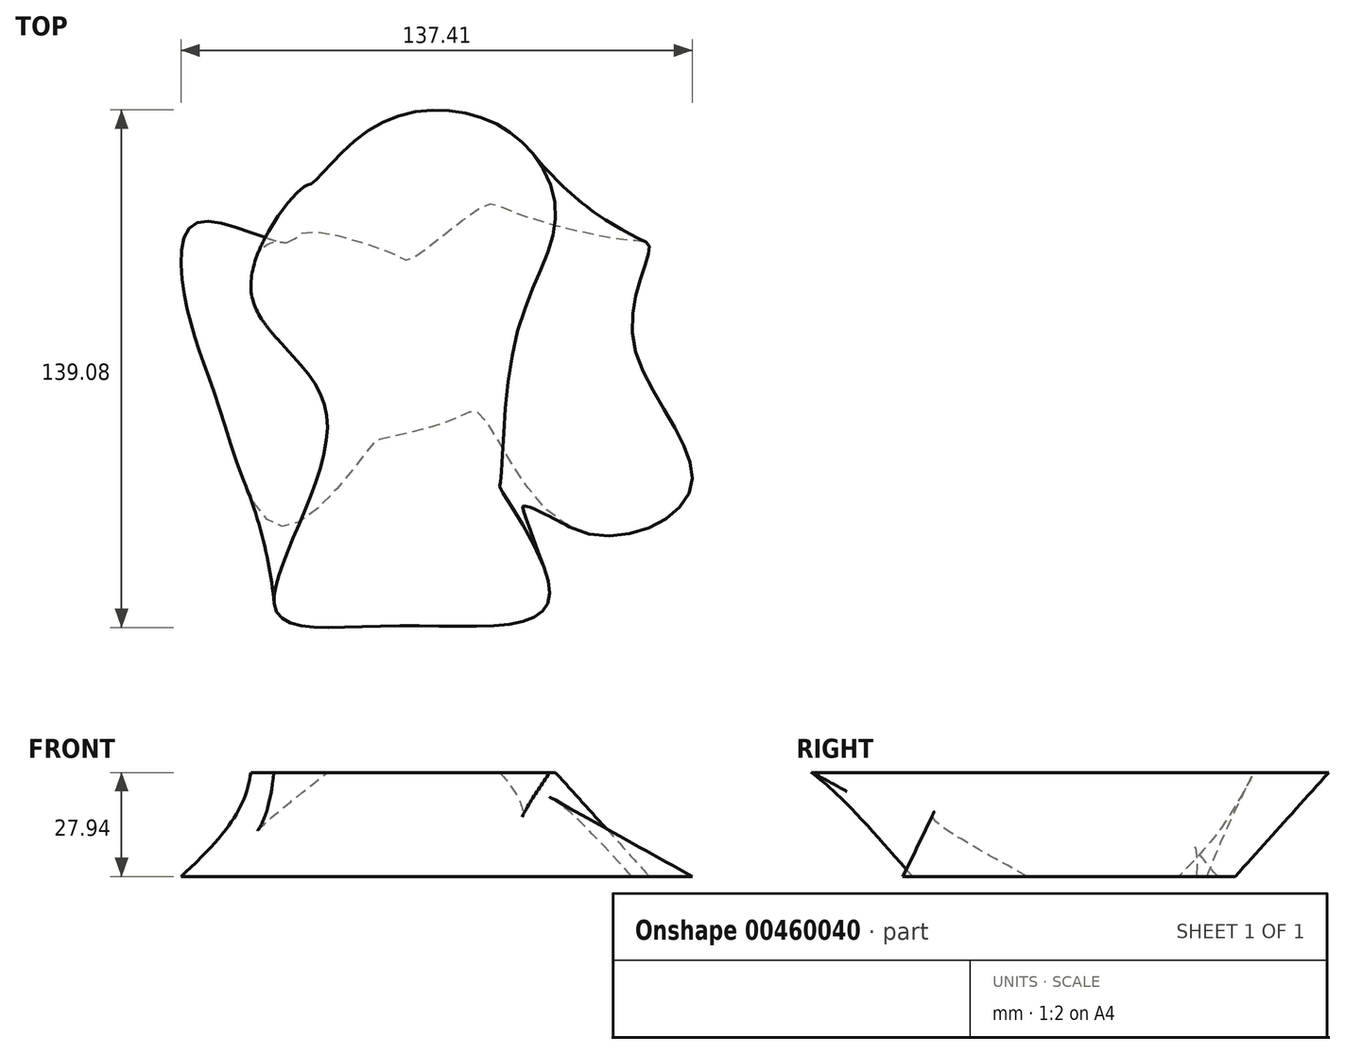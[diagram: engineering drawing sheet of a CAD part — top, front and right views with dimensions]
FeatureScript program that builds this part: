
annotation { "Feature Type Name" : "Feature", "Feature Type Description" : "" }
export const myFeature = defineFeature(function(context is Context, id is Id, definition is map)
    precondition{}
    {
        {
            var Q0;
            Q0=qCreatedBy(makeId("Top.planeOp"),FACE);
            var sketch = newSketch(context, id + "F0", { "sketchPlane" : qUnion([Q0])});
            skFitSpline(sketch, "E0", {"points": [v(-33.51, 29.77) * mm, v(-28.86, 32.46) * mm, v(-3.32, 25.96) * mm, v(0, 25.4) * mm, v(19.83, 39.8) * mm, v(25.33, 38.8) * mm, v(56.94, 30.62) * mm, v(63.85, 28.79) * mm, v(59.48, 3.67) * mm, v(75.14, -35.84) * mm, v(43.4, -47.13) * mm, v(18.13, -16.23) * mm, v(11.64, -17.64) * mm, v(-7.83, -23) * mm, v(-11.22, -25.26) * mm, v(-34.22, -46.57) * mm, v(-51.15, -16.37) * mm, v(-60.75, 13.97) * mm, v(-57.5, 35.14) * mm, v(-33.51, 29.77) * mm]});
            skSolve(sketch);
        }
        {
            var Q0;
            Q0=qCreatedBy(makeId("Top.planeOp"),FACE);
            cPlane(context, id + "F1", {"entities" : qUnion([Q0]), "cplaneType" : CPlaneType.OFFSET, "offset" : 27.94 * mm, "width" : 152.4 * mm, "height" : 152.4 * mm});
        }
        {
            var Q0;
            Q0=qCreatedBy(id+"F1.planeOp",FACE);
            var sketch = newSketch(context, id + "F2", { "sketchPlane" : qUnion([Q0])});
            skFitSpline(sketch, "E1", {"points": [v(-28.65, 45.01) * mm, v(-27.1, 45.44) * mm, v(-8.89, 61.52) * mm, v(25.4, 60.11) * mm, v(38.66, 36.83) * mm, v(28.08, 4.37) * mm, v(23.85, -35) * mm, v(23.85, -36.27) * mm, v(36.97, -66.04) * mm, v(-3.95, -73.24) * mm, v(-36.83, -68.16) * mm, v(-22.86, -16.5) * mm, v(-43.18, 16.93) * mm, v(-28.65, 45.01) * mm]});
            skSolve(sketch);
        }
        {
            var Q0;
            Q0=makeQuery(id+"F0.imprint","IMPRINT",FACE,{"disambiguationData":[TD([[makeQuery(id+"F0.imprint","IMPRINT",EDGE,{"derivedFrom":sQuery(id+"F0.wireOp",EDGE,"E0")}),-1.0]])]});
            var Q1;
            Q1=makeQuery(id+"F2.imprint","IMPRINT",FACE,{"disambiguationData":[TD([[makeQuery(id+"F2.imprint","IMPRINT",EDGE,{"derivedFrom":sQuery(id+"F2.wireOp",EDGE,"E1")}),-1.0]])]});
            loft(context, id + "F3", {"sheetProfilesArray" : [{ "sheetProfileEntities" : qUnion([Q0]) }, { "sheetProfileEntities" : qUnion([Q1]) }]});
        }
    });
